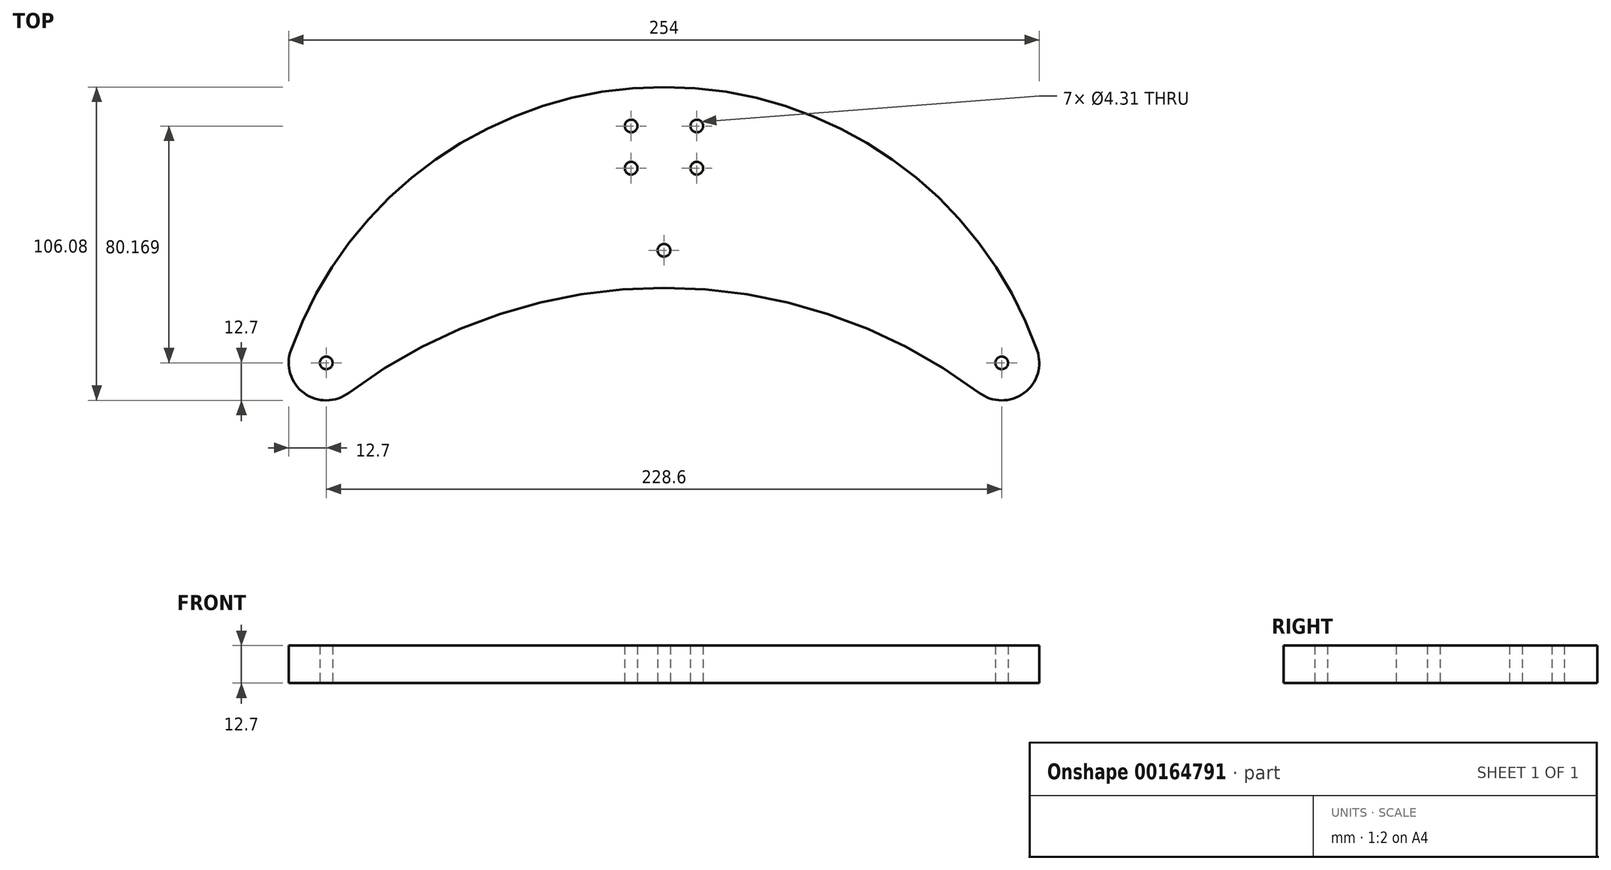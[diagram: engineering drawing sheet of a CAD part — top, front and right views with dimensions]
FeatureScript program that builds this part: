
annotation { "Feature Type Name" : "Feature", "Feature Type Description" : "" }
export const myFeature = defineFeature(function(context is Context, id is Id, definition is map)
    precondition{}
    {
        {
            var Q0;
            Q0=qCreatedBy(makeId("Top.planeOp"),FACE);
            var sketch = newSketch(context, id + "F0", { "sketchPlane" : qUnion([Q0])});
            skLineSegment(sketch, "E0", {"start": v(0, 0) * mm, "end": v(254, 0) * mm, "construction": true});
            skLineSegment(sketch, "E1", {"start": v(127, 0) * mm, "end": v(127, 0) * mm});
            skLineSegment(sketch, "E2", {"start": v(0, 0) * mm, "end": v(0, -254) * mm});
            skLineSegment(sketch, "E3", {"start": v(254, 0) * mm, "end": v(254, -254) * mm});
            skArc(sketch, "E4", {"start": v(233.68, -10.16) * mm, "mid": v(127, 25.4) * mm, "end": v(20.32, -10.16) * mm});
            skLineSegment(sketch, "E5", {"start": v(127, 0) * mm, "end": v(127, -152.4) * mm, "construction": true});
            skCircle(sketch, "E6", {"center": v(127, 38.1) * mm, "radius": 12.7 * mm, "construction": true});
            skCircle(sketch, "E7", {"center": v(12.7, 0) * mm, "radius": 2.15 * mm});
            skCircle(sketch, "E8", {"center": v(127, 38.1) * mm, "radius": 2.15 * mm});
            skCircle(sketch, "E9", {"center": v(241.3, 0) * mm, "radius": 2.15 * mm});
            skLineSegment(sketch, "E10", {"start": v(0, 0) * mm, "end": v(0, 0) * mm});
            skLineSegment(sketch, "E11", {"start": v(254, 0) * mm, "end": v(254, 0) * mm});
            skArc(sketch, "E12", {"start": v(0.73, 4.25) * mm, "mid": v(5.17, -10.23) * mm, "end": v(20.32, -10.16) * mm});
            skArc(sketch, "E13", {"start": v(233.68, -10.16) * mm, "mid": v(248.83, -10.23) * mm, "end": v(253.27, 4.25) * mm});
            skArc(sketch, "E14", {"start": v(253.27, 4.25) * mm, "mid": v(127, 93.38) * mm, "end": v(0.73, 4.25) * mm});
            skLineSegment(sketch, "E15.bottom", {"start": v(138.11, 65.88) * mm, "end": v(115.89, 65.88) * mm, "construction": true});
            skLineSegment(sketch, "E15.top", {"start": v(138.11, 80.17) * mm, "end": v(115.89, 80.17) * mm, "construction": true});
            skLineSegment(sketch, "E15.left", {"start": v(138.11, 65.88) * mm, "end": v(138.11, 80.17) * mm, "construction": true});
            skLineSegment(sketch, "E15.right", {"start": v(115.89, 65.88) * mm, "end": v(115.89, 80.17) * mm, "construction": true});
            skPoint(sketch, "E15.middle", {"position": v(127, 73.03) * mm});
            skLineSegment(sketch, "E16", {"start": v(127, 38.1) * mm, "end": v(127, 0) * mm, "construction": true});
            skLineSegment(sketch, "E17", {"start": v(127, 38.1) * mm, "end": v(127, 73.03) * mm, "construction": true});
            skCircle(sketch, "E18", {"center": v(115.89, 80.17) * mm, "radius": 12.7 * mm, "construction": true});
            skCircle(sketch, "E19", {"center": v(115.89, 80.17) * mm, "radius": 2.15 * mm});
            skCircle(sketch, "E20", {"center": v(138.11, 80.17) * mm, "radius": 2.15 * mm});
            skCircle(sketch, "E21", {"center": v(138.11, 65.88) * mm, "radius": 2.15 * mm});
            skCircle(sketch, "E22", {"center": v(115.89, 65.88) * mm, "radius": 2.15 * mm});
            skSolve(sketch);
        }
        {
            var Q0;
            Q0 = qSketchRegion(id + "F0", true);
            extrude(context, id + "F1", {"entities" : qUnion([Q0]), "depth" : 12.7 * mm});
        }
    });
